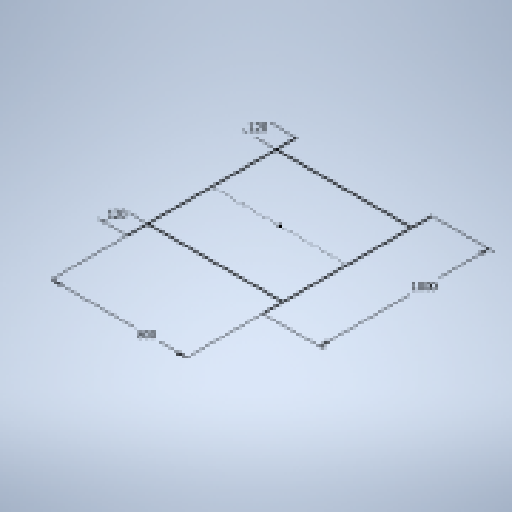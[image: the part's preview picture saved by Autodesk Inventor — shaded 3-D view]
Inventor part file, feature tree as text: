
AUTODESK INVENTOR PART (.ipt)
format: ipt  version: 2025 (Build 290162010, 162A)  size: 132,608 bytes
history: native  units: mm
features: sketch x1
ambient origin geometry x8: Origin, YZ Plane, XZ Plane, XY Plane, X Axis, Y Axis, Z Axis, Center Point
feature tree (1):
  sketch  "Sketch1"  dims[d0=800.0mm d1=1000.0mm d2=120.0mm d3=120.0mm]
